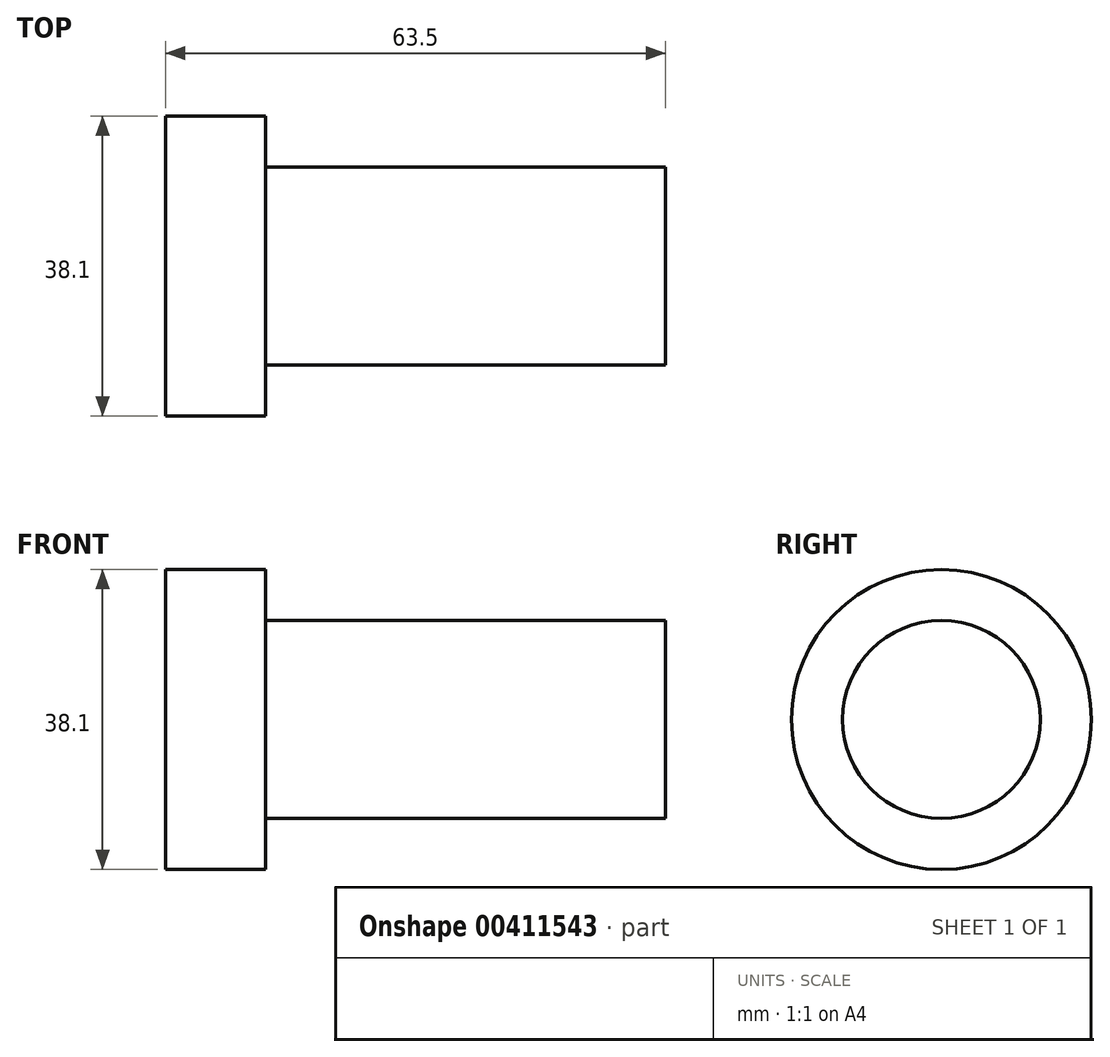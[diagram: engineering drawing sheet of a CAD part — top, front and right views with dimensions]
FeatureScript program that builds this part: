
annotation { "Feature Type Name" : "Feature", "Feature Type Description" : "" }
export const myFeature = defineFeature(function(context is Context, id is Id, definition is map)
    precondition{}
    {
        {
            var Q0;
            Q0=qCreatedBy(makeId("Top.planeOp"),FACE);
            var sketch = newSketch(context, id + "F0", { "sketchPlane" : qUnion([Q0])});
            skLineSegment(sketch, "E0", {"start": v(-18.36, 0) * mm, "end": v(-18.36, 19.05) * mm});
            skLineSegment(sketch, "E1", {"start": v(-18.36, 19.05) * mm, "end": v(-5.66, 19.05) * mm});
            skLineSegment(sketch, "E2", {"start": v(-5.66, 19.05) * mm, "end": v(-5.66, 12.57) * mm});
            skLineSegment(sketch, "E3", {"start": v(-5.66, 12.57) * mm, "end": v(45.14, 12.57) * mm});
            skLineSegment(sketch, "E4", {"start": v(45.14, 12.57) * mm, "end": v(45.14, 0) * mm});
            skLineSegment(sketch, "E5", {"start": v(-18.36, 0) * mm, "end": v(45.14, 0) * mm, "construction": true});
            skLineSegment(sketch, "E6", {"start": v(-18.36, 0) * mm, "end": v(45.14, 0) * mm});
            skSolve(sketch);
        }
        {
            var Q0;
            Q0=makeQuery(id+"F0.imprint","IMPRINT",FACE,{"disambiguationData":[TD([[makeQuery(id+"F0.imprint","IMPRINT",EDGE,{"derivedFrom":sQuery(id+"F0.wireOp",EDGE,"E0")}),-1.0]])]});
            var Q1;
            Q1=sQuery(id+"F0.wireOp",EDGE,"E6");
            revolve(context, id + "F1", {"entities" : qUnion([Q0]), "axis" : qUnion([Q1]), "revolveType" : RevolveType.FULL});
        }
    });
